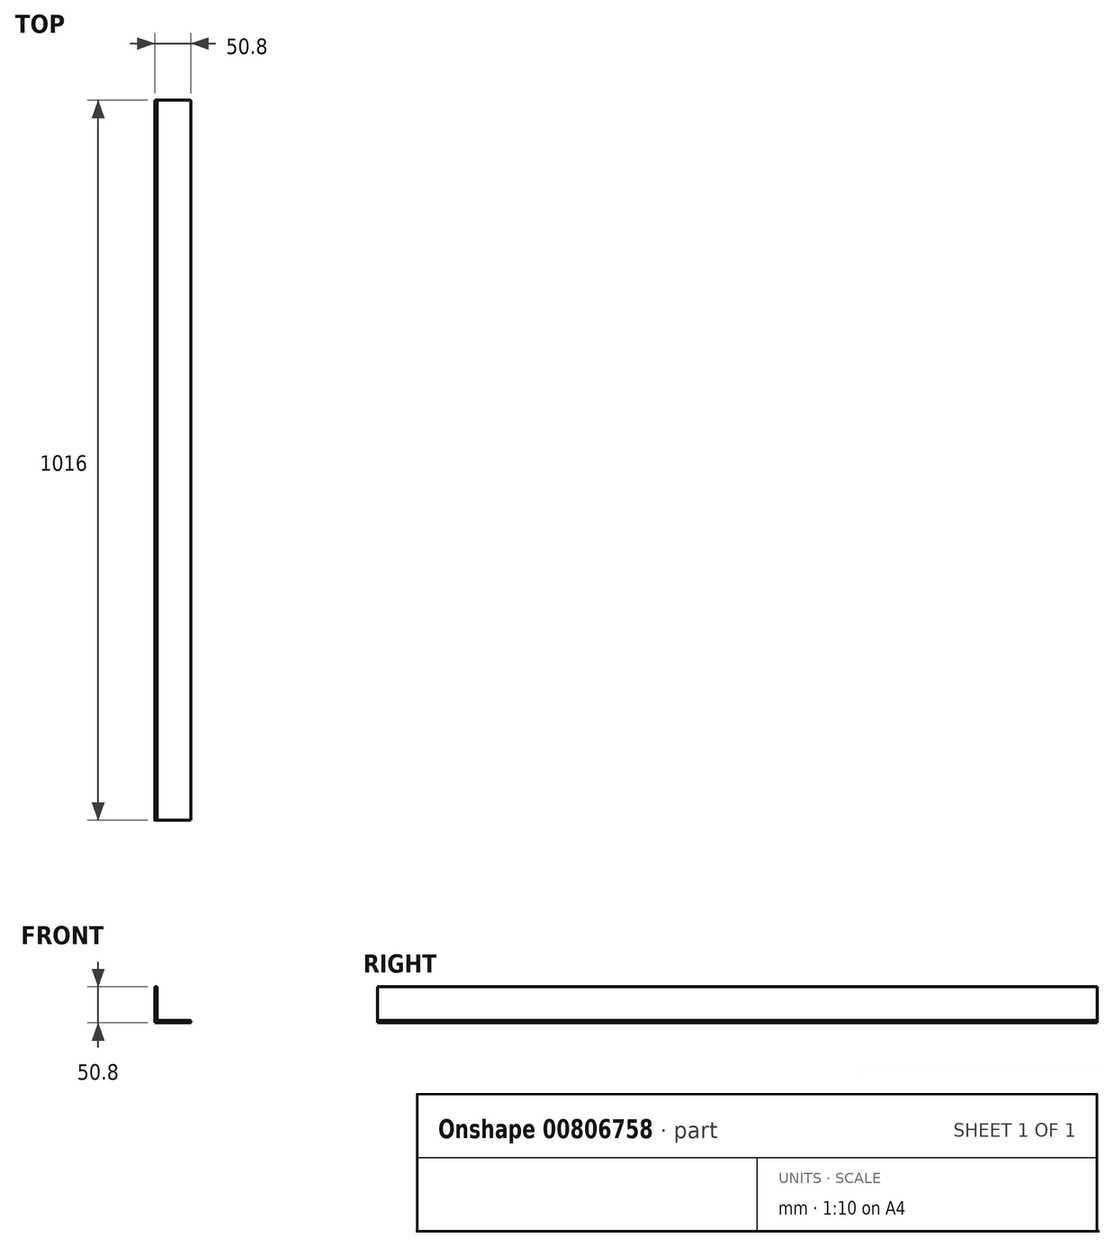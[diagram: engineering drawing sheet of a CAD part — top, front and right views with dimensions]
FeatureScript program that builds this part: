
annotation { "Feature Type Name" : "Feature", "Feature Type Description" : "" }
export const myFeature = defineFeature(function(context is Context, id is Id, definition is map)
    precondition{}
    {
        {
            var Q0;
            Q0=qCreatedBy(makeId("Front.planeOp"),FACE);
            var sketch = newSketch(context, id + "F0", { "sketchPlane" : qUnion([Q0])});
            skLineSegment(sketch, "E0.bottom", {"start": v(0, 0) * mm, "end": v(50.04, 0) * mm});
            skLineSegment(sketch, "E0.top", {"start": v(0.76, 50.8) * mm, "end": v(2.41, 50.8) * mm});
            skLineSegment(sketch, "E0.left", {"start": v(0, 0) * mm, "end": v(0, 50.04) * mm});
            skLineSegment(sketch, "E0.right", {"start": v(50.8, 0.76) * mm, "end": v(50.8, 2.41) * mm});
            skLineSegment(sketch, "E1.0", {"start": v(3.17, 6.35) * mm, "end": v(3.17, 50.04) * mm});
            skLineSegment(sketch, "E1.1", {"start": v(6.35, 3.18) * mm, "end": v(50.04, 3.18) * mm});
            skPoint(sketch, "E2.visualSharp", {"position": v(0, 50.8) * mm});
            skArc(sketch, "E2.filletArc", {"start": v(0.76, 50.8) * mm, "mid": v(0.22, 50.58) * mm, "end": v(0, 50.04) * mm});
            skPoint(sketch, "E3.visualSharp", {"position": v(50.8, 0) * mm});
            skArc(sketch, "E3.filletArc", {"start": v(50.04, 0) * mm, "mid": v(50.58, 0.22) * mm, "end": v(50.8, 0.76) * mm});
            skPoint(sketch, "E4.visualSharp", {"position": v(50.8, 3.18) * mm});
            skArc(sketch, "E4.filletArc", {"start": v(50.8, 2.41) * mm, "mid": v(50.58, 2.95) * mm, "end": v(50.04, 3.18) * mm});
            skPoint(sketch, "E5.visualSharp", {"position": v(3.18, 50.8) * mm});
            skArc(sketch, "E5.filletArc", {"start": v(3.18, 50.04) * mm, "mid": v(2.95, 50.58) * mm, "end": v(2.41, 50.8) * mm});
            skPoint(sketch, "E6.visualSharp", {"position": v(3.17, 3.18) * mm});
            skArc(sketch, "E6.filletArc", {"start": v(3.18, 6.35) * mm, "mid": v(4.1, 4.1) * mm, "end": v(6.35, 3.17) * mm});
            skSolve(sketch);
        }
        {
            var Q0;
            Q0 = qSketchRegion(id + "F0", true);
            extrude(context, id + "F1", {"entities" : qUnion([Q0]), "depth" : 1016 * mm, "offsetDistance" : 25.4 * mm});
        }
    });
